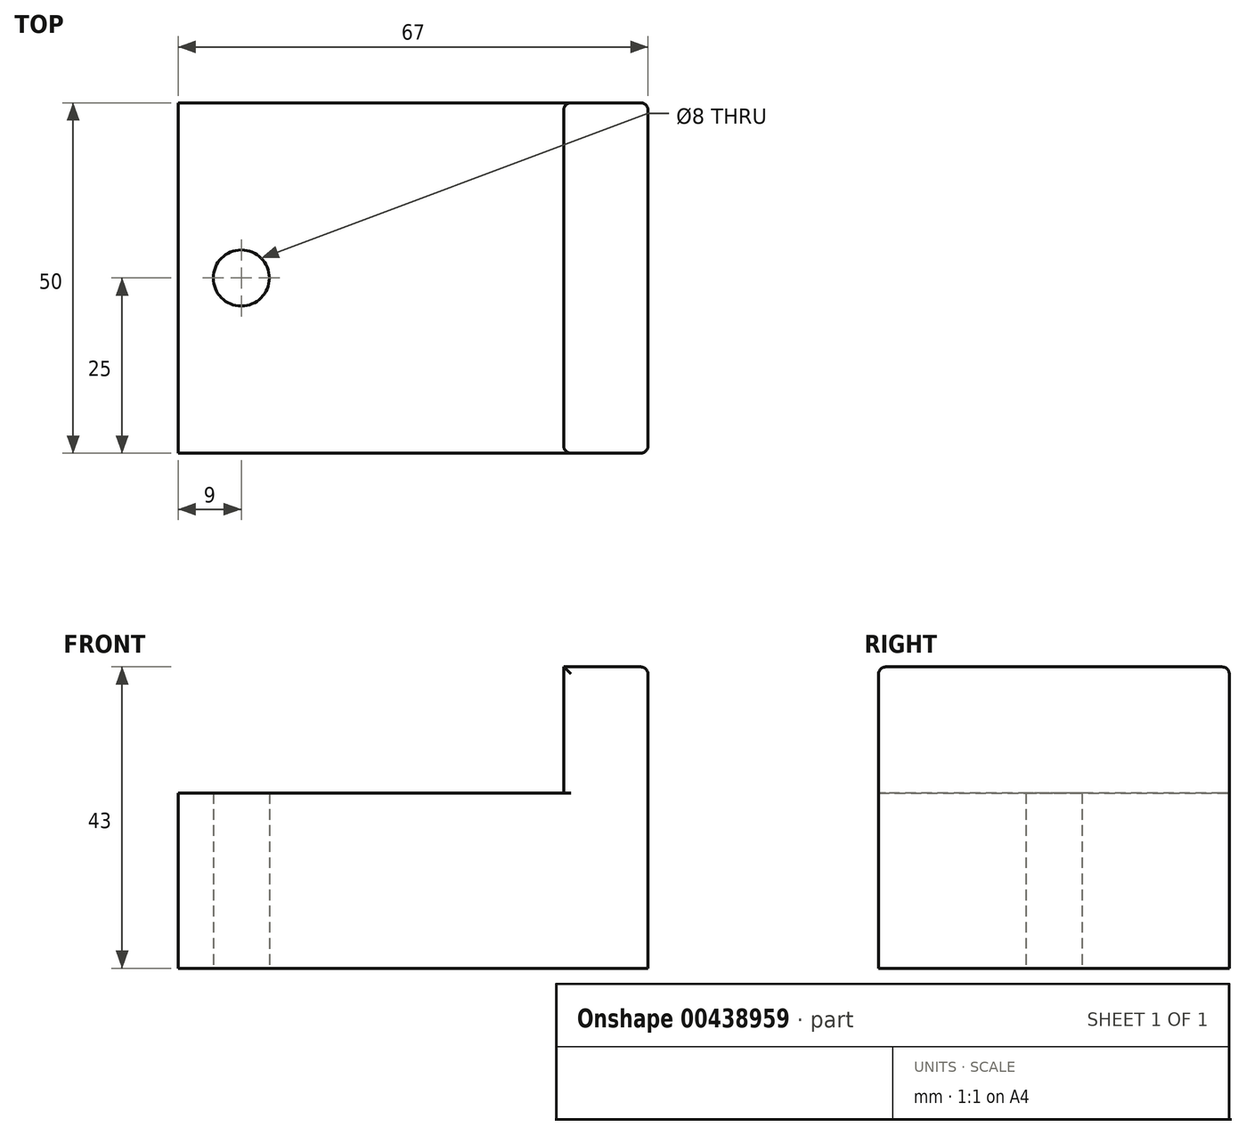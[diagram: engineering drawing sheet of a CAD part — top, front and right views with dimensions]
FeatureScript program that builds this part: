
annotation { "Feature Type Name" : "Feature", "Feature Type Description" : "" }
export const myFeature = defineFeature(function(context is Context, id is Id, definition is map)
    precondition{}
    {
        {
            var Q0;
            Q0=qCreatedBy(makeId("Top.planeOp"),FACE);
            var sketch = newSketch(context, id + "F0", { "sketchPlane" : qUnion([Q0])});
            skLineSegment(sketch, "E0.bottom", {"start": v(27.5, -25) * mm, "end": v(-27.5, -25) * mm});
            skLineSegment(sketch, "E0.top", {"start": v(27.5, 25) * mm, "end": v(-27.5, 25) * mm});
            skLineSegment(sketch, "E0.left", {"start": v(27.5, -25) * mm, "end": v(27.5, 25) * mm});
            skLineSegment(sketch, "E0.right", {"start": v(-27.5, -25) * mm, "end": v(-27.5, 25) * mm});
            skPoint(sketch, "E0.middle", {"position": v(0, 0) * mm});
            skLineSegment(sketch, "E1.bottom", {"start": v(27.5, 25) * mm, "end": v(39.5, 25) * mm});
            skLineSegment(sketch, "E1.top", {"start": v(27.5, -25) * mm, "end": v(39.5, -25) * mm});
            skLineSegment(sketch, "E1.left", {"start": v(27.5, 25) * mm, "end": v(27.5, -25) * mm});
            skLineSegment(sketch, "E1.right", {"start": v(39.5, 25) * mm, "end": v(39.5, -25) * mm});
            skCircle(sketch, "E2", {"center": v(-18.5, 0) * mm, "radius": 4 * mm});
            skSolve(sketch);
        }
        {
            var Q0;
            Q0 = qSketchRegion(id + "F0", true);
            extrude(context, id + "F1", {"entities" : qUnion([Q0]), "depth" : 25 * mm});
        }
        {
            var Q0;
            {var subQ3=sQuery(id+"F0.wireOp",EDGE,"E1.bottom");Q0=makeQuery(id+"F0.imprint","IMPRINT",FACE,{"disambiguationData":[TD([[makeQuery(id+"F0.imprint","IMPRINT",EDGE,{"derivedFrom":subQ3}),-1.0]])]});}
            extrude(context, id + "F2", {"entities" : qUnion([Q0]), "operationType" : NewBodyOperationType.ADD, "depth" : 43 * mm});
        }
        {
            var Q0;
            Q0=makeQuery(id+"F2.opExtrude","SWEPT_EDGE",EDGE,{"disambiguationData":[OSD([sQuery(id+"F0.wireOp",EDGE,"E0.top"),sQuery(id+"F0.wireOp",EDGE,"E1.bottom"),sQuery(id+"F0.wireOp",EDGE,"E1.left")])]});
            var Q1;
            Q1=makeQuery(id+"F2.opExtrude","CAP_EDGE",EDGE,{"disambiguationData":[OSD([sQuery(id+"F0.wireOp",EDGE,"E1.bottom")])],"isStart":false});
            var Q2;
            {var subQ0=sQuery(id+"F0.wireOp",EDGE,"E1.right");var subQ1=sQuery(id+"F0.wireOp",EDGE,"E1.bottom");Q2=makeQuery(id+"F2.boolean.opBoolean","MERGE",EDGE,{"derivedFrom":[makeQuery(id+"F1.opExtrude","SWEPT_EDGE",EDGE,{"disambiguationData":[OSD([subQ1,subQ0])]}),makeQuery(id+"F2.opExtrude","SWEPT_EDGE",EDGE,{"disambiguationData":[OSD([subQ1,subQ0])]})]});}
            var Q3;
            Q3=makeQuery(id+"F2.opExtrude","CAP_EDGE",EDGE,{"disambiguationData":[OSD([sQuery(id+"F0.wireOp",EDGE,"E1.right")])],"isStart":false});
            var Q4;
            Q4=makeQuery(id+"F2.opExtrude","CAP_EDGE",EDGE,{"disambiguationData":[OSD([sQuery(id+"F0.wireOp",EDGE,"E1.left")])],"isStart":false});
            var Q5;
            Q5=makeQuery(id+"F2.opExtrude","CAP_EDGE",EDGE,{"disambiguationData":[OSD([sQuery(id+"F0.wireOp",EDGE,"E1.top")])],"isStart":false});
            var Q6;
            Q6=makeQuery(id+"F2.opExtrude","SWEPT_EDGE",EDGE,{"disambiguationData":[OSD([sQuery(id+"F0.wireOp",EDGE,"E0.bottom"),sQuery(id+"F0.wireOp",EDGE,"E1.top"),sQuery(id+"F0.wireOp",EDGE,"E1.left")])]});
            var Q7;
            {var subQ0=sQuery(id+"F0.wireOp",EDGE,"E1.right");var subQ1=sQuery(id+"F0.wireOp",EDGE,"E1.top");Q7=makeQuery(id+"F2.boolean.opBoolean","MERGE",EDGE,{"derivedFrom":[makeQuery(id+"F1.opExtrude","SWEPT_EDGE",EDGE,{"disambiguationData":[OSD([subQ1,subQ0])]}),makeQuery(id+"F2.opExtrude","SWEPT_EDGE",EDGE,{"disambiguationData":[OSD([subQ1,subQ0])]})]});}
            fillet(context, id + "F3", {"entities" : qUnion([Q0, Q1, Q2, Q3, Q4, Q5, Q6, Q7]), "radius" : 1 * mm, "tangentPropagation" : true, "allowEdgeOverflow" : false});
        }
    });
